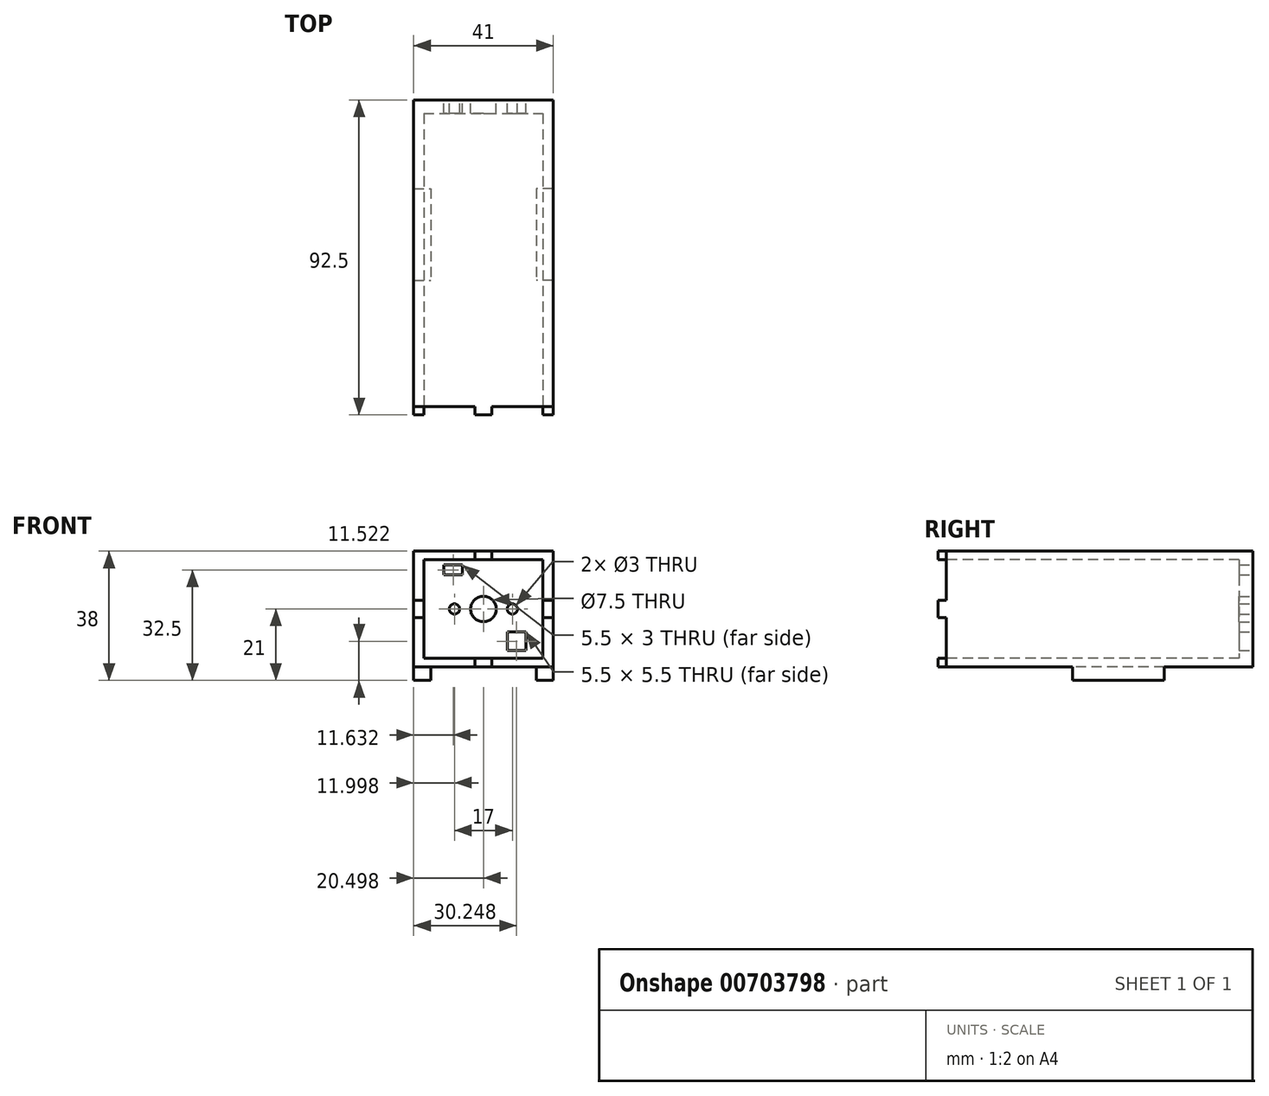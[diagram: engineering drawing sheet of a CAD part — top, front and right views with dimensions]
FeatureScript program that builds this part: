
annotation { "Feature Type Name" : "Feature", "Feature Type Description" : "" }
export const myFeature = defineFeature(function(context is Context, id is Id, definition is map)
    precondition{}
    {
        {
            var Q0;
            Q0=qCreatedBy(makeId("Top.planeOp"),FACE);
            var sketch = newSketch(context, id + "F0", { "sketchPlane" : qUnion([Q0])});
            skLineSegment(sketch, "E0.bottom", {"start": v(-22.2, 49.2) * mm, "end": v(18.8, 49.2) * mm});
            skLineSegment(sketch, "E0.top", {"start": v(-22.2, -40.8) * mm, "end": v(18.8, -40.8) * mm});
            skLineSegment(sketch, "E0.left", {"start": v(-22.2, 49.2) * mm, "end": v(-22.2, -40.8) * mm});
            skLineSegment(sketch, "E0.right", {"start": v(18.8, 49.2) * mm, "end": v(18.8, -40.8) * mm});
            skSolve(sketch);
        }
        {
            var Q0;
            Q0=makeQuery(id+"F0.imprint","IMPRINT",FACE,{"disambiguationData":[TD([[makeQuery(id+"F0.imprint","IMPRINT",EDGE,{"derivedFrom":sQuery(id+"F0.wireOp",EDGE,"E0.bottom")}),-1.0]])]});
            extrude(context, id + "F1", {"entities" : qUnion([Q0]), "depth" : 34 * mm, "offsetDistance" : 25 * mm});
        }
        {
            var Q0;
            Q0=makeQuery(id+"F1.opExtrude","SWEPT_FACE",FACE,{"disambiguationData":[OSD([sQuery(id+"F0.wireOp",EDGE,"E0.top")])]});
            var sketch = newSketch(context, id + "F2", { "sketchPlane" : qUnion([Q0])});
            skLineSegment(sketch, "E1.bottom", {"start": v(-19.2, 31.5) * mm, "end": v(15.8, 31.5) * mm});
            skLineSegment(sketch, "E1.top", {"start": v(-19.2, 2.5) * mm, "end": v(15.8, 2.5) * mm});
            skLineSegment(sketch, "E1.left", {"start": v(-19.2, 31.5) * mm, "end": v(-19.2, 2.5) * mm});
            skLineSegment(sketch, "E1.right", {"start": v(15.8, 31.5) * mm, "end": v(15.8, 2.5) * mm});
            skSolve(sketch);
        }
        {
            var Q0;
            Q0=makeQuery(id+"F2.imprint","IMPRINT",FACE,{"disambiguationData":[TD([[makeQuery(id+"F2.imprint","IMPRINT",EDGE,{"derivedFrom":sQuery(id+"F2.wireOp",EDGE,"E1.bottom")}),-1.0]])]});
            extrude(context, id + "F3", {"entities" : qUnion([Q0]), "operationType" : NewBodyOperationType.REMOVE, "oppositeDirection" : true, "depth" : 86 * mm, "offsetDistance" : 25 * mm});
        }
        {
            var Q0;
            Q0=makeQuery(id+"F1.opExtrude","SWEPT_FACE",FACE,{"disambiguationData":[OSD([sQuery(id+"F0.wireOp",EDGE,"E0.bottom")])]});
            var sketch = newSketch(context, id + "F4", { "sketchPlane" : qUnion([Q0])});
            skCircle(sketch, "E2", {"center": v(1.7, 17) * mm, "radius": 3.75 * mm});
            skCircle(sketch, "E3", {"center": v(-6.8, 17) * mm, "radius": 1.5 * mm});
            skCircle(sketch, "E4", {"center": v(10.2, 17) * mm, "radius": 1.5 * mm});
            skLineSegment(sketch, "E5.bottom", {"start": v(7.82, 30) * mm, "end": v(13.32, 30) * mm});
            skLineSegment(sketch, "E5.top", {"start": v(7.82, 27) * mm, "end": v(13.32, 27) * mm});
            skLineSegment(sketch, "E5.left", {"start": v(7.82, 30) * mm, "end": v(7.82, 27) * mm});
            skLineSegment(sketch, "E5.right", {"start": v(13.32, 30) * mm, "end": v(13.32, 27) * mm});
            skLineSegment(sketch, "E6.bottom", {"start": v(-10.8, 10.27) * mm, "end": v(-5.3, 10.27) * mm});
            skLineSegment(sketch, "E6.top", {"start": v(-10.8, 4.77) * mm, "end": v(-5.3, 4.77) * mm});
            skLineSegment(sketch, "E6.left", {"start": v(-10.8, 10.27) * mm, "end": v(-10.8, 4.77) * mm});
            skLineSegment(sketch, "E6.right", {"start": v(-5.3, 10.27) * mm, "end": v(-5.3, 4.77) * mm});
            skSolve(sketch);
        }
        {
            var Q0;
            Q0=makeQuery(id+"F4.imprint","IMPRINT",FACE,{"disambiguationData":[TD([[makeQuery(id+"F4.imprint","IMPRINT",EDGE,{"derivedFrom":sQuery(id+"F4.wireOp",EDGE,"E6.bottom")}),-1.0]])]});
            var Q1;
            Q1=makeQuery(id+"F4.imprint","IMPRINT",FACE,{"disambiguationData":[TD([[makeQuery(id+"F4.imprint","IMPRINT",EDGE,{"derivedFrom":sQuery(id+"F4.wireOp",EDGE,"E2")}),1.0]])]});
            var Q2;
            Q2=makeQuery(id+"F4.imprint","IMPRINT",FACE,{"disambiguationData":[TD([[makeQuery(id+"F4.imprint","IMPRINT",EDGE,{"derivedFrom":sQuery(id+"F4.wireOp",EDGE,"E5.bottom")}),-1.0]])]});
            var Q3;
            Q3=makeQuery(id+"F4.imprint","IMPRINT",FACE,{"disambiguationData":[TD([[makeQuery(id+"F4.imprint","IMPRINT",EDGE,{"derivedFrom":sQuery(id+"F4.wireOp",EDGE,"E4")}),1.0]])]});
            var Q4;
            Q4=makeQuery(id+"F4.imprint","IMPRINT",FACE,{"disambiguationData":[TD([[makeQuery(id+"F4.imprint","IMPRINT",EDGE,{"derivedFrom":sQuery(id+"F4.wireOp",EDGE,"E3")}),1.0]])]});
            extrude(context, id + "F5", {"entities" : qUnion([Q0, Q1, Q2, Q3, Q4]), "operationType" : NewBodyOperationType.REMOVE, "endBound" : BoundingType.UP_TO_NEXT, "oppositeDirection" : true, "depth" : 25 * mm, "offsetDistance" : 25 * mm});
        }
        {
            var Q0;
            Q0=makeQuery(id+"F1.opExtrude","SWEPT_FACE",FACE,{"disambiguationData":[OSD([sQuery(id+"F0.wireOp",EDGE,"E0.top")])]});
            var sketch = newSketch(context, id + "F6", { "sketchPlane" : qUnion([Q0])});
            skLineSegment(sketch, "E7.bottom", {"start": v(-4.2, 34) * mm, "end": v(0.8, 34) * mm});
            skLineSegment(sketch, "E7.top", {"start": v(-4.2, 31.5) * mm, "end": v(0.8, 31.5) * mm});
            skLineSegment(sketch, "E7.left", {"start": v(-4.2, 34) * mm, "end": v(-4.2, 31.5) * mm});
            skLineSegment(sketch, "E7.right", {"start": v(0.8, 34) * mm, "end": v(0.8, 31.5) * mm});
            skLineSegment(sketch, "E8.bottom", {"start": v(-4.2, 2.5) * mm, "end": v(0.8, 2.5) * mm});
            skLineSegment(sketch, "E8.top", {"start": v(-4.2, 0) * mm, "end": v(0.8, 0) * mm});
            skLineSegment(sketch, "E8.left", {"start": v(-4.2, 2.5) * mm, "end": v(-4.2, 0) * mm});
            skLineSegment(sketch, "E8.right", {"start": v(0.8, 2.5) * mm, "end": v(0.8, 0) * mm});
            skLineSegment(sketch, "E9.bottom", {"start": v(-22.2, 19.5) * mm, "end": v(-19.2, 19.5) * mm});
            skLineSegment(sketch, "E9.top", {"start": v(-22.2, 14.5) * mm, "end": v(-19.2, 14.5) * mm});
            skLineSegment(sketch, "E9.left", {"start": v(-22.2, 19.5) * mm, "end": v(-22.2, 14.5) * mm});
            skLineSegment(sketch, "E9.right", {"start": v(-19.2, 19.5) * mm, "end": v(-19.2, 14.5) * mm});
            skLineSegment(sketch, "E10.bottom", {"start": v(15.8, 19.5) * mm, "end": v(18.8, 19.5) * mm});
            skLineSegment(sketch, "E10.top", {"start": v(15.8, 14.5) * mm, "end": v(18.8, 14.5) * mm});
            skLineSegment(sketch, "E10.left", {"start": v(15.8, 19.5) * mm, "end": v(15.8, 14.5) * mm});
            skLineSegment(sketch, "E10.right", {"start": v(18.8, 19.5) * mm, "end": v(18.8, 14.5) * mm});
            skSolve(sketch);
        }
        {
            var Q0;
            Q0=makeQuery(id+"F6.imprint","IMPRINT",FACE,{"disambiguationData":[TD([[makeQuery(id+"F6.imprint","IMPRINT",EDGE,{"derivedFrom":sQuery(id+"F6.wireOp",EDGE,"E7.bottom")}),-1.0]])]});
            var Q1;
            Q1=makeQuery(id+"F6.imprint","IMPRINT",FACE,{"disambiguationData":[TD([[makeQuery(id+"F6.imprint","IMPRINT",EDGE,{"derivedFrom":sQuery(id+"F6.wireOp",EDGE,"E9.bottom")}),-1.0]])]});
            var Q2;
            Q2=makeQuery(id+"F6.imprint","IMPRINT",FACE,{"disambiguationData":[TD([[makeQuery(id+"F6.imprint","IMPRINT",EDGE,{"derivedFrom":sQuery(id+"F6.wireOp",EDGE,"E10.bottom")}),-1.0]])]});
            var Q3;
            Q3=makeQuery(id+"F6.imprint","IMPRINT",FACE,{"disambiguationData":[TD([[makeQuery(id+"F6.imprint","IMPRINT",EDGE,{"derivedFrom":sQuery(id+"F6.wireOp",EDGE,"E8.bottom")}),-1.0]])]});
            extrude(context, id + "F7", {"entities" : qUnion([Q0, Q1, Q2, Q3]), "operationType" : NewBodyOperationType.ADD, "depth" : 2.5 * mm, "offsetDistance" : 25 * mm});
        }
        {
            var Q0;
            Q0=makeQuery(id+"F7.boolean.opBoolean","MERGE",FACE,{"derivedFrom":[makeQuery(id+"F1.opExtrude","CAP_FACE",FACE,{"disambiguationData":[OSD([sQuery(id+"F0.wireOp",EDGE,"E0.bottom"),sQuery(id+"F0.wireOp",EDGE,"E0.top"),sQuery(id+"F0.wireOp",EDGE,"E0.left"),sQuery(id+"F0.wireOp",EDGE,"E0.right")])],"isStart":true}),makeQuery(id+"F7.opExtrude","SWEPT_FACE",FACE,{"disambiguationData":[OSD([sQuery(id+"F6.wireOp",EDGE,"E8.top")])]})]});
            var sketch = newSketch(context, id + "F8", { "sketchPlane" : qUnion([Q0])});
            skLineSegment(sketch, "E11.bottom", {"start": v(18.8, -23.2) * mm, "end": v(13.8, -23.2) * mm});
            skLineSegment(sketch, "E11.top", {"start": v(18.8, 3.8) * mm, "end": v(13.8, 3.8) * mm});
            skLineSegment(sketch, "E11.left", {"start": v(18.8, -23.2) * mm, "end": v(18.8, 3.8) * mm});
            skLineSegment(sketch, "E11.right", {"start": v(13.8, -23.2) * mm, "end": v(13.8, 3.8) * mm});
            skLineSegment(sketch, "E12.bottom", {"start": v(-22.2, -23.2) * mm, "end": v(-17.2, -23.2) * mm});
            skLineSegment(sketch, "E12.top", {"start": v(-22.2, 3.8) * mm, "end": v(-17.2, 3.8) * mm});
            skLineSegment(sketch, "E12.left", {"start": v(-22.2, -23.2) * mm, "end": v(-22.2, 3.8) * mm});
            skLineSegment(sketch, "E12.right", {"start": v(-17.2, -23.2) * mm, "end": v(-17.2, 3.8) * mm});
            skSolve(sketch);
        }
        {
            var Q0;
            Q0=makeQuery(id+"F8.imprint","IMPRINT",FACE,{"disambiguationData":[TD([[makeQuery(id+"F8.imprint","IMPRINT",EDGE,{"derivedFrom":sQuery(id+"F8.wireOp",EDGE,"E12.bottom")}),1.0]])]});
            var Q1;
            Q1=makeQuery(id+"F8.imprint","IMPRINT",FACE,{"disambiguationData":[TD([[makeQuery(id+"F8.imprint","IMPRINT",EDGE,{"derivedFrom":sQuery(id+"F8.wireOp",EDGE,"E11.bottom")}),-1.0]])]});
            extrude(context, id + "F9", {"entities" : qUnion([Q0, Q1]), "operationType" : NewBodyOperationType.ADD, "depth" : 4 * mm, "offsetDistance" : 25 * mm});
        }
    });
